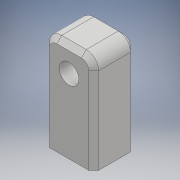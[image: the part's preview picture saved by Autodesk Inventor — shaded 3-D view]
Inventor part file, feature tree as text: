
AUTODESK INVENTOR PART (.ipt)
format: ipt  version: 2017 (Build 210142000, 142)  size: 192,000 bytes
history: native  units: mm
features: extrude x6, sketch x5, chamfer x3, projected_geometry x2, fillet x1
ambient origin geometry x8: Origin, YZ Plane, XZ Plane, XY Plane, X Axis, Y Axis, Z Axis, Center Point
bodies: Solid1 (feature_tree)
feature tree (17):
  sketch  "Sketch1"  dims[d0=15.0mm d1=20.0mm]
  extrude  "Extrusion1"  Depth=20.0mm
  extrude  "Extrusion2"  Depth=15.0mm TaperAngle=0.0deg
  extrude  "Extrusion3"  Depth=10.0mm
  fillet  "Fillet1"  Radius=10.0mm
  extrude  "Extrusion4"  Depth=5.0mm
  chamfer  "Chamfer1"  Distance=25.0mm
  chamfer  "Chamfer2"  Distance=2.0mm Angle=45.0deg
  extrude  "Extrusion5"  Depth=4.0mm TaperAngle=45.0deg
  extrude  "Extrusion6"  TaperAngle=0.0deg  [1 undecoded]
  chamfer  "Chamfer3"  Distance=5.0mm
  sketch  "Sketch2"  dims[d2=6.0mm d3=15.0mm d4=0.0mm]
  sketch  "Sketch3"  dims[d5=25.0mm d6=0.0mm d7=8.0mm d8=10.0mm]
  sketch  "Sketch4"  dims[d9=25.0mm d10=0.0mm d11=5.0mm]
  projected_geometry  "Projected Loop1"
  sketch  "Sketch5"  dims[d12=4.3mm d13=25.0mm d14=0.0mm d15=2.0mm d16=2.0mm d17=45.0deg d18=4.0mm d19=2.0mm d20=45.0deg d21=0.0mm d22=0.0mm d23=5.0mm d24=5.0mm d25=10.0mm d26=0.0mm d27=2.0mm d28=2.0mm d29=45.0deg]
  projected_geometry  "Projected Loop2"
note: 1 required parameter value undecoded (feature->parameter linkage not recoverable at this tier; creation-order binding heuristic only, values carry confidence <= 0.55)
